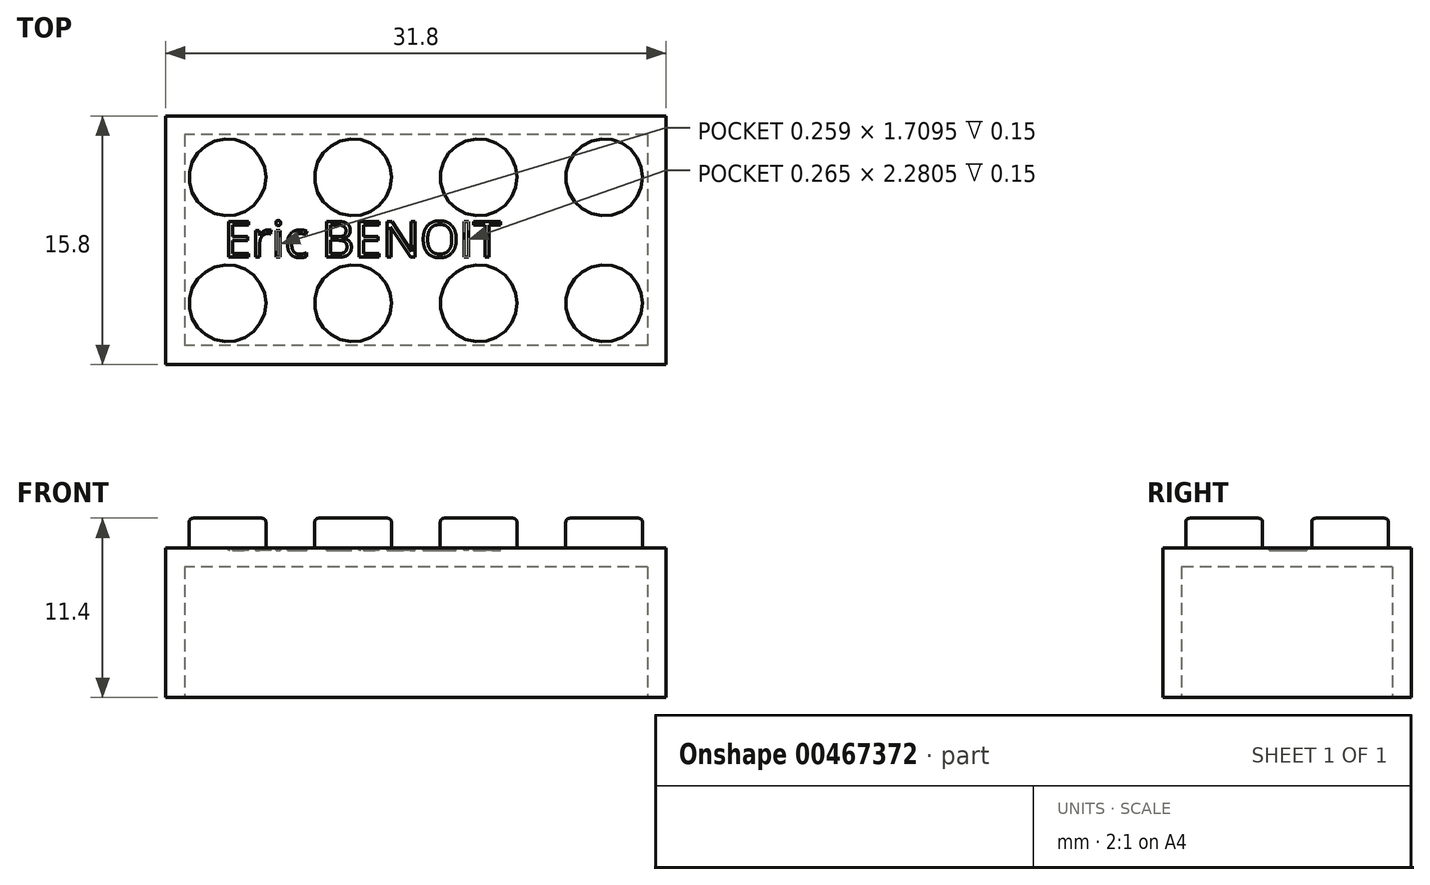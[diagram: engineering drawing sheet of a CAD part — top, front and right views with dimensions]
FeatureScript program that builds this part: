
annotation { "Feature Type Name" : "Feature", "Feature Type Description" : "" }
export const myFeature = defineFeature(function(context is Context, id is Id, definition is map)
    precondition{}
    {
        {
            var Q0;
            Q0=qCreatedBy(makeId("Top.planeOp"),FACE);
            var sketch = newSketch(context, id + "F0", { "sketchPlane" : qUnion([Q0])});
            skLineSegment(sketch, "E0.bottom", {"start": v(15.9, 7.9) * mm, "end": v(-15.9, 7.9) * mm});
            skLineSegment(sketch, "E0.top", {"start": v(15.9, -7.9) * mm, "end": v(-15.9, -7.9) * mm});
            skLineSegment(sketch, "E0.left", {"start": v(15.9, 7.9) * mm, "end": v(15.9, -7.9) * mm});
            skLineSegment(sketch, "E0.right", {"start": v(-15.9, 7.9) * mm, "end": v(-15.9, -7.9) * mm});
            skPoint(sketch, "E0.middle", {"position": v(0, 0) * mm});
            skSolve(sketch);
        }
        {
            var Q0;
            Q0=makeQuery(id+"F0.imprint","IMPRINT",FACE,{"disambiguationData":[TD([[makeQuery(id+"F0.imprint","IMPRINT",EDGE,{"derivedFrom":sQuery(id+"F0.wireOp",EDGE,"E0.bottom")}),1.0]])]});
            extrude(context, id + "F1", {"entities" : qUnion([Q0]), "depth" : 9.5 * mm});
        }
        {
            var Q0;
            Q0=makeQuery(id+"F1.opExtrude","CAP_FACE",FACE,{"disambiguationData":[OSD([sQuery(id+"F0.wireOp",EDGE,"E0.bottom"),sQuery(id+"F0.wireOp",EDGE,"E0.top"),sQuery(id+"F0.wireOp",EDGE,"E0.left"),sQuery(id+"F0.wireOp",EDGE,"E0.right")])],"isStart":true});
            shell(context, id + "F2", {"entities" : qUnion([Q0]), "thickness" : 1.2 * mm});
        }
        {
            var Q0;
            Q0=makeQuery(id+"F1.opExtrude","CAP_FACE",FACE,{"disambiguationData":[OSD([sQuery(id+"F0.wireOp",EDGE,"E0.bottom"),sQuery(id+"F0.wireOp",EDGE,"E0.top"),sQuery(id+"F0.wireOp",EDGE,"E0.left"),sQuery(id+"F0.wireOp",EDGE,"E0.right")])],"isStart":false});
            var sketch = newSketch(context, id + "F3", { "sketchPlane" : qUnion([Q0])});
            skPoint(sketch, "E1.middle", {"position": v(0, 0) * mm});
            skCircle(sketch, "E2", {"center": v(11.96, 4) * mm, "radius": 2.44 * mm});
            skCircle(sketch, "E3", {"center": v(3.99, 4) * mm, "radius": 2.44 * mm});
            skCircle(sketch, "E4", {"center": v(3.99, -4) * mm, "radius": 2.44 * mm});
            skCircle(sketch, "E5", {"center": v(11.96, -4) * mm, "radius": 2.44 * mm});
            skCircle(sketch, "E6", {"center": v(-3.99, 4) * mm, "radius": 2.44 * mm});
            skCircle(sketch, "E7", {"center": v(-3.99, -4) * mm, "radius": 2.44 * mm});
            skCircle(sketch, "E8", {"center": v(-11.96, -4) * mm, "radius": 2.44 * mm});
            skCircle(sketch, "E9", {"center": v(-11.96, 4) * mm, "radius": 2.44 * mm});
            skSolve(sketch);
        }
        {
            var Q0;
            Q0=makeQuery(id+"F3.imprint","IMPRINT",FACE,{"disambiguationData":[TD([[makeQuery(id+"F3.imprint","IMPRINT",EDGE,{"derivedFrom":sQuery(id+"F3.wireOp",EDGE,"E9")}),1.0]])]});
            var Q1;
            Q1=makeQuery(id+"F3.imprint","IMPRINT",FACE,{"disambiguationData":[TD([[makeQuery(id+"F3.imprint","IMPRINT",EDGE,{"derivedFrom":sQuery(id+"F3.wireOp",EDGE,"E6")}),1.0]])]});
            var Q2;
            Q2=makeQuery(id+"F3.imprint","IMPRINT",FACE,{"disambiguationData":[TD([[makeQuery(id+"F3.imprint","IMPRINT",EDGE,{"derivedFrom":sQuery(id+"F3.wireOp",EDGE,"E3")}),1.0]])]});
            var Q3;
            Q3=makeQuery(id+"F3.imprint","IMPRINT",FACE,{"disambiguationData":[TD([[makeQuery(id+"F3.imprint","IMPRINT",EDGE,{"derivedFrom":sQuery(id+"F3.wireOp",EDGE,"E2")}),1.0]])]});
            var Q4;
            Q4=makeQuery(id+"F3.imprint","IMPRINT",FACE,{"disambiguationData":[TD([[makeQuery(id+"F3.imprint","IMPRINT",EDGE,{"derivedFrom":sQuery(id+"F3.wireOp",EDGE,"E5")}),1.0]])]});
            var Q5;
            Q5=makeQuery(id+"F3.imprint","IMPRINT",FACE,{"disambiguationData":[TD([[makeQuery(id+"F3.imprint","IMPRINT",EDGE,{"derivedFrom":sQuery(id+"F3.wireOp",EDGE,"E4")}),1.0]])]});
            var Q6;
            Q6=makeQuery(id+"F3.imprint","IMPRINT",FACE,{"disambiguationData":[TD([[makeQuery(id+"F3.imprint","IMPRINT",EDGE,{"derivedFrom":sQuery(id+"F3.wireOp",EDGE,"E7")}),1.0]])]});
            var Q7;
            Q7=makeQuery(id+"F3.imprint","IMPRINT",FACE,{"disambiguationData":[TD([[makeQuery(id+"F3.imprint","IMPRINT",EDGE,{"derivedFrom":sQuery(id+"F3.wireOp",EDGE,"E8")}),1.0]])]});
            var Q8;
            Q8=sQuery(id+"F3.wireOp",EDGE,"E9");
            var Q9;
            Q9=sQuery(id+"F3.wireOp",EDGE,"E6");
            var Q10;
            Q10=sQuery(id+"F3.wireOp",EDGE,"E3");
            var Q11;
            Q11=sQuery(id+"F3.wireOp",EDGE,"E2");
            var Q12;
            Q12=sQuery(id+"F3.wireOp",EDGE,"E4");
            var Q13;
            Q13=sQuery(id+"F3.wireOp",EDGE,"E5");
            var Q14;
            Q14=sQuery(id+"F3.wireOp",EDGE,"E7");
            var Q15;
            Q15=sQuery(id+"F3.wireOp",EDGE,"E8");
            extrude(context, id + "F4", {"entities" : qUnion([Q0, Q1, Q2, Q3, Q4, Q5, Q6, Q7]), "surfaceEntities" : qUnion([Q8, Q9, Q10, Q11, Q12, Q13, Q14, Q15]), "depth" : 1.9 * mm});
        }
        {
            var Q0;
            Q0=makeQuery(id+"F4.opExtrude","CAP_FACE",FACE,{"disambiguationData":[OSD([sQuery(id+"F3.wireOp",EDGE,"E9")])],"isStart":false});
            var Q1;
            Q1=makeQuery(id+"F4.opExtrude","CAP_FACE",FACE,{"disambiguationData":[OSD([sQuery(id+"F3.wireOp",EDGE,"E6")])],"isStart":false});
            var Q2;
            Q2=makeQuery(id+"F4.opExtrude","CAP_FACE",FACE,{"disambiguationData":[OSD([sQuery(id+"F3.wireOp",EDGE,"E3")])],"isStart":false});
            var Q3;
            Q3=makeQuery(id+"F4.opExtrude","CAP_FACE",FACE,{"disambiguationData":[OSD([sQuery(id+"F3.wireOp",EDGE,"E2")])],"isStart":false});
            var Q4;
            Q4=makeQuery(id+"F4.opExtrude","CAP_FACE",FACE,{"disambiguationData":[OSD([sQuery(id+"F3.wireOp",EDGE,"E5")])],"isStart":false});
            var Q5;
            Q5=makeQuery(id+"F4.opExtrude","CAP_FACE",FACE,{"disambiguationData":[OSD([sQuery(id+"F3.wireOp",EDGE,"E4")])],"isStart":false});
            var Q6;
            Q6=makeQuery(id+"F4.opExtrude","CAP_FACE",FACE,{"disambiguationData":[OSD([sQuery(id+"F3.wireOp",EDGE,"E7")])],"isStart":false});
            var Q7;
            Q7=makeQuery(id+"F4.opExtrude","CAP_FACE",FACE,{"disambiguationData":[OSD([sQuery(id+"F3.wireOp",EDGE,"E8")])],"isStart":false});
            fillet(context, id + "F5", {"entities" : qUnion([Q0, Q1, Q2, Q3, Q4, Q5, Q6, Q7]), "radius" : 0.3 * mm, "tangentPropagation" : true, "rho" : 0.5, "crossSection" : FilletCrossSection.CONIC, "allowEdgeOverflow" : false});
        }
        {
            var Q0;
            Q0=makeQuery(id+"F1.opExtrude","CAP_FACE",FACE,{"disambiguationData":[OSD([sQuery(id+"F0.wireOp",EDGE,"E0.bottom"),sQuery(id+"F0.wireOp",EDGE,"E0.top"),sQuery(id+"F0.wireOp",EDGE,"E0.left"),sQuery(id+"F0.wireOp",EDGE,"E0.right")])],"isStart":false});
            var sketch = newSketch(context, id + "F6", { "sketchPlane" : qUnion([Q0])});
            skText(sketch, "E10", { "text": "Eric BENOIT", "fontName": "OpenSans-Regular.ttf"});
            const initialGuessF6  = {"E10": [-0.01222, -0.00108, 1, 0, 0.0023]};
            skSetInitialGuess(sketch, initialGuessF6);
            skSolve(sketch);
        }
        {
            var Q0;
            Q0 = qSketchRegion(id + "F6", true);
            extrude(context, id + "F7", {"entities" : qUnion([Q0]), "operationType" : NewBodyOperationType.REMOVE, "oppositeDirection" : true, "depth" : 0.15 * mm});
        }
    });
